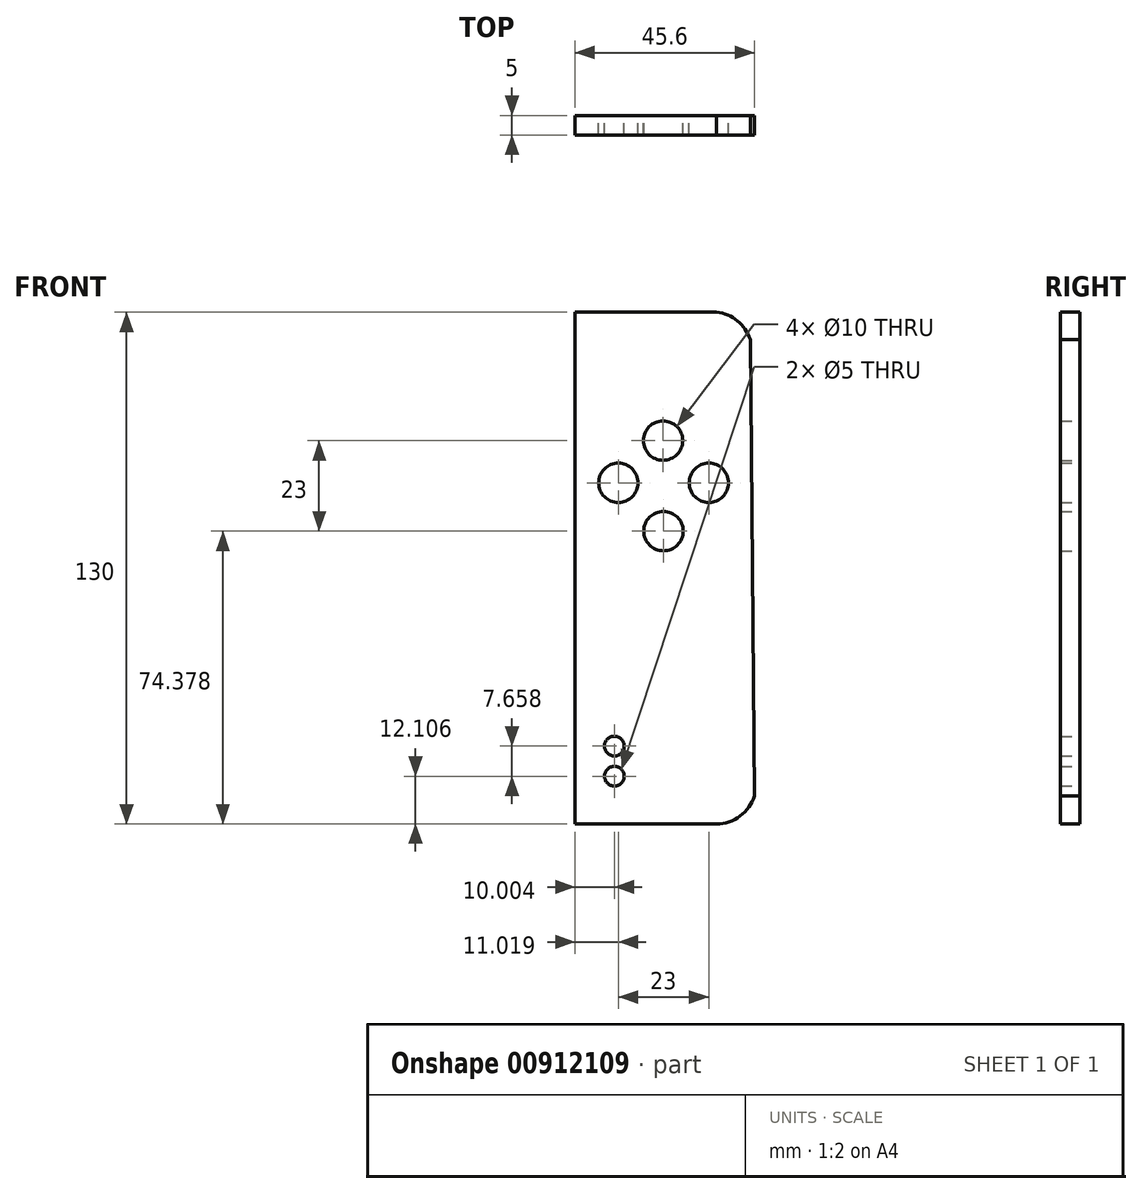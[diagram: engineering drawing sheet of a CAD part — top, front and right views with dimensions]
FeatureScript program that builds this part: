
annotation { "Feature Type Name" : "Feature", "Feature Type Description" : "" }
export const myFeature = defineFeature(function(context is Context, id is Id, definition is map)
    precondition{}
    {
        {
            var Q0;
            Q0=qCreatedBy(makeId("Front.planeOp"),FACE);
            var sketch = newSketch(context, id + "F0", { "sketchPlane" : qUnion([Q0])});
            skLineSegment(sketch, "E0", {"start": v(22.4, 65.02) * mm, "end": v(-13.56, 65.02) * mm});
            skArc(sketch, "E1", {"start": v(-13.56, 65.02) * mm, "mid": v(-19.56, 63.03) * mm, "end": v(-23.19, 57.86) * mm});
            skLineSegment(sketch, "E2", {"start": v(-13.56, -64.98) * mm, "end": v(22.4, -64.98) * mm});
            skArc(sketch, "E3", {"start": v(-22.1, -58.06) * mm, "mid": v(-18.86, -62.8) * mm, "end": v(-13.56, -64.98) * mm});
            skLineSegment(sketch, "E4", {"start": v(-23.19, 57.86) * mm, "end": v(-22.1, -58.06) * mm});
            skLineSegment(sketch, "E5", {"start": v(22.4, 65.02) * mm, "end": v(22.4, -64.98) * mm});
            skPoint(sketch, "E6.endSnap0", {"position": v(22.4, 0.02) * mm});
            skLineSegment(sketch, "E7.top", {"start": v(-2.94, 10.9) * mm, "end": v(3.06, 10.9) * mm});
            skLineSegment(sketch, "E7.left", {"start": v(-2.94, 2.9) * mm, "end": v(-2.94, 10.9) * mm});
            skLineSegment(sketch, "E7.right", {"start": v(3.06, 2.9) * mm, "end": v(3.06, 10.9) * mm});
            skLineSegment(sketch, "E8.top", {"start": v(3.06, -11.1) * mm, "end": v(-2.94, -11.1) * mm});
            skLineSegment(sketch, "E8.left", {"start": v(3.06, -3.1) * mm, "end": v(3.06, -11.1) * mm});
            skLineSegment(sketch, "E8.right", {"start": v(-2.94, -3.1) * mm, "end": v(-2.94, -11.1) * mm});
            skPoint(sketch, "E9", {"position": v(3.06, 2.9) * mm});
            skPoint(sketch, "E10", {"position": v(3.06, -3.1) * mm});
            skLineSegment(sketch, "E11.bottom", {"start": v(3.06, 2.9) * mm, "end": v(10.83, 2.9) * mm});
            skLineSegment(sketch, "E11.top", {"start": v(3.06, -3.1) * mm, "end": v(10.83, -3.1) * mm});
            skLineSegment(sketch, "E11.right", {"start": v(10.83, 2.9) * mm, "end": v(10.83, -3.1) * mm});
            skLineSegment(sketch, "E12.bottom", {"start": v(-2.94, -3.1) * mm, "end": v(-10.7, -3.1) * mm});
            skLineSegment(sketch, "E12.top", {"start": v(-2.94, 2.9) * mm, "end": v(-10.7, 2.9) * mm});
            skLineSegment(sketch, "E12.right", {"start": v(-10.7, -3.1) * mm, "end": v(-10.7, 2.9) * mm});
            skPoint(sketch, "E13.trimOffspring.end.orphan", {"position": v(22.4, 1.44) * mm});
            skPoint(sketch, "E6.start.orphan", {"position": v(-22.65, -0.1) * mm});
            skLineSegment(sketch, "E14", {"start": v(135.28, -198.32) * mm, "end": v(171.25, -198.32) * mm});
            skArc(sketch, "E15", {"start": v(171.25, -198.32) * mm, "mid": v(177.25, -196.34) * mm, "end": v(180.88, -191.16) * mm});
            skLineSegment(sketch, "E16", {"start": v(171.25, -68.32) * mm, "end": v(135.28, -68.32) * mm});
            skArc(sketch, "E17", {"start": v(179.8, -75.24) * mm, "mid": v(176.56, -70.51) * mm, "end": v(171.25, -68.32) * mm});
            skLineSegment(sketch, "E18", {"start": v(180.88, -191.16) * mm, "end": v(179.8, -75.24) * mm});
            skLineSegment(sketch, "E19", {"start": v(135.28, -198.32) * mm, "end": v(135.28, -68.32) * mm});
            skPoint(sketch, "E20.endSnap0", {"position": v(135.28, -133.32) * mm});
            skPoint(sketch, "E21.trimOffspring.end.orphan", {"position": v(135.28, -134.75) * mm});
            skPoint(sketch, "E20.start.orphan", {"position": v(180.34, -133.2) * mm});
            skCircle(sketch, "E22", {"center": v(157.66, -100.94) * mm, "radius": 5 * mm});
            skCircle(sketch, "E23", {"center": v(157.77, -123.94) * mm, "radius": 5 * mm});
            skLineSegment(sketch, "E24", {"start": v(157.31, -68.32) * mm, "end": v(157.31, -198.32) * mm});
            skPoint(sketch, "E24.endSnap0", {"position": v(153.27, -198.32) * mm});
            skCircle(sketch, "E25", {"center": v(146.3, -111.68) * mm, "radius": 5 * mm});
            skCircle(sketch, "E26", {"center": v(169.3, -111.68) * mm, "radius": 5 * mm});
            skCircle(sketch, "E27", {"center": v(145.28, -178.56) * mm, "radius": 2.5 * mm});
            skCircle(sketch, "E28", {"center": v(145.28, -186.21) * mm, "radius": 2.5 * mm});
            skSolve(sketch);
        }
        {
            var Q0;
            {var subQ11=sQuery(id+"F0.wireOp",EDGE,"E19");Q0=makeQuery(id+"F0.imprint","IMPRINT",FACE,{"disambiguationData":[TD([[makeQuery(id+"F0.imprint","IMPRINT",EDGE,{"derivedFrom":subQ11}),-1.0]])]});}
            var Q1;
            {var subQ9=sQuery(id+"F0.wireOp",EDGE,"E15");Q1=makeQuery(id+"F0.imprint","IMPRINT",FACE,{"disambiguationData":[TD([[makeQuery(id+"F0.imprint","IMPRINT",EDGE,{"derivedFrom":subQ9}),1.0]])]});}
            extrude(context, id + "F1", {"entities" : qUnion([Q0, Q1]), "depth" : 5 * mm, "offsetDistance" : 25 * mm});
        }
    });
